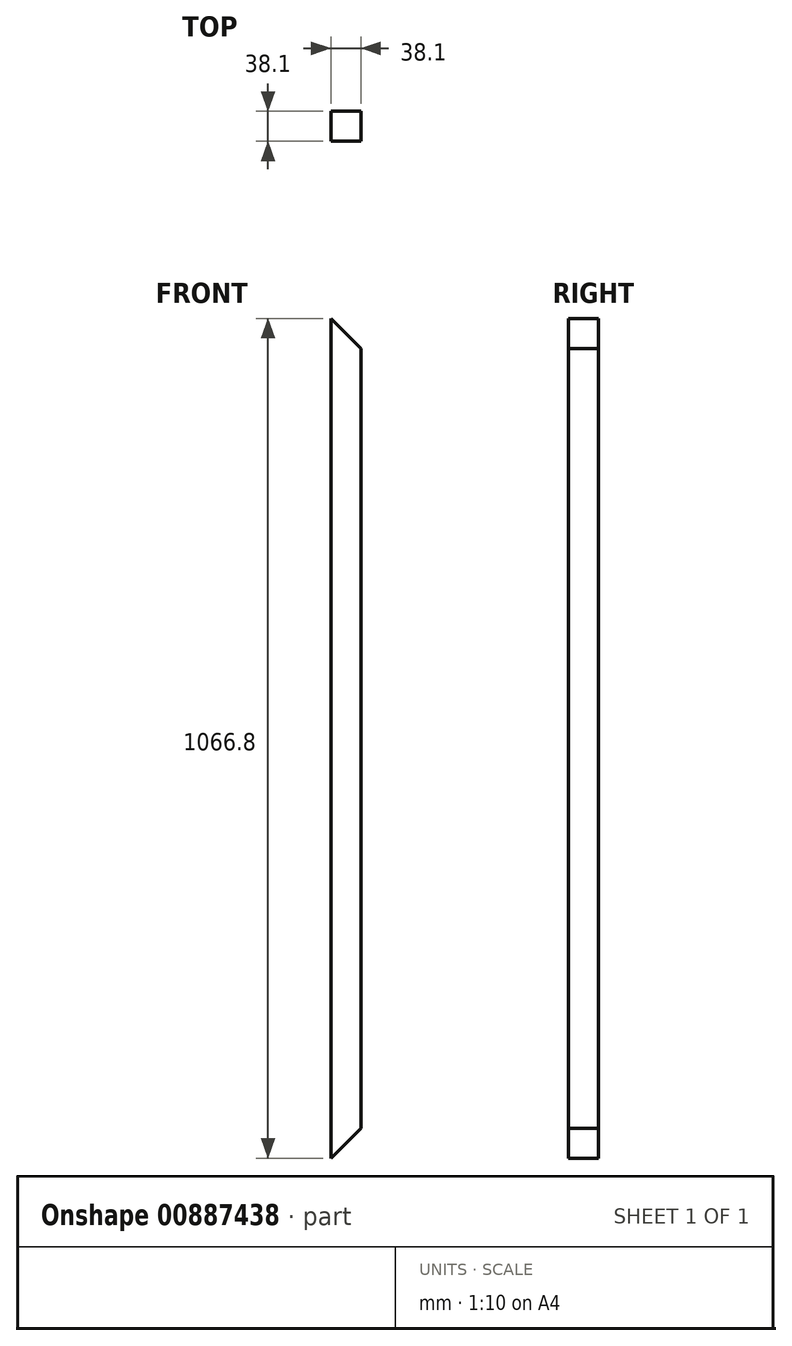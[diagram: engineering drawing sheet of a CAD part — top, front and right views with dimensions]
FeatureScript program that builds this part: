
annotation { "Feature Type Name" : "Feature", "Feature Type Description" : "" }
export const myFeature = defineFeature(function(context is Context, id is Id, definition is map)
    precondition{}
    {
        {
            var Q0;
            Q0=qCreatedBy(makeId("Top.planeOp"),FACE);
            var sketch = newSketch(context, id + "F0", { "sketchPlane" : qUnion([Q0])});
            skLineSegment(sketch, "E0.bottom", {"start": v(19.05, 19.05) * mm, "end": v(-19.05, 19.05) * mm});
            skLineSegment(sketch, "E0.top", {"start": v(19.05, -19.05) * mm, "end": v(-19.05, -19.05) * mm});
            skLineSegment(sketch, "E0.left", {"start": v(19.05, 19.05) * mm, "end": v(19.05, -19.05) * mm});
            skLineSegment(sketch, "E0.right", {"start": v(-19.05, 19.05) * mm, "end": v(-19.05, -19.05) * mm});
            skPoint(sketch, "E0.middle", {"position": v(0, 0) * mm});
            skSolve(sketch);
        }
        {
            var Q0;
            Q0=makeQuery(id+"F0.imprint","IMPRINT",FACE,{"disambiguationData":[TD([[makeQuery(id+"F0.imprint","IMPRINT",EDGE,{"derivedFrom":sQuery(id+"F0.wireOp",EDGE,"E0.bottom")}),1.0]])]});
            extrude(context, id + "F1", {"entities" : qUnion([Q0]), "depth" : 1066.8 * mm, "offsetDistance" : 25.4 * mm});
        }
        {
            var Q0;
            Q0=makeQuery(id+"F1.opExtrude","SWEPT_FACE",FACE,{"disambiguationData":[OSD([sQuery(id+"F0.wireOp",EDGE,"E0.top")])]});
            var sketch = newSketch(context, id + "F2", { "sketchPlane" : qUnion([Q0])});
            skLineSegment(sketch, "E1", {"start": v(-19.05, 1066.8) * mm, "end": v(19.05, 1028.7) * mm});
            skLineSegment(sketch, "E2", {"start": v(19.05, 38.1) * mm, "end": v(-19.05, 0) * mm});
            skSolve(sketch);
        }
        {
            var Q0;
            {var subQ0=sQuery(id+"F2.wireOp",EDGE,"E1");Q0=makeQuery(id+"F2.imprint","IMPRINT",FACE,{"disambiguationData":[TD([[makeQuery(id+"F2.imprint","IMPRINT",EDGE,{"derivedFrom":subQ0}),1.0]])]});}
            extrude(context, id + "F3", {"entities" : qUnion([Q0]), "operationType" : NewBodyOperationType.REMOVE, "oppositeDirection" : true, "depth" : 38.1 * mm, "offsetDistance" : 25.4 * mm});
        }
        {
            var Q0;
            {var subQ0=sQuery(id+"F2.wireOp",EDGE,"E2");Q0=makeQuery(id+"F2.imprint","IMPRINT",FACE,{"disambiguationData":[TD([[makeQuery(id+"F2.imprint","IMPRINT",EDGE,{"derivedFrom":subQ0}),1.0]])]});}
            extrude(context, id + "F4", {"entities" : qUnion([Q0]), "operationType" : NewBodyOperationType.REMOVE, "oppositeDirection" : true, "depth" : 38.1 * mm, "offsetDistance" : 25.4 * mm});
        }
    });
